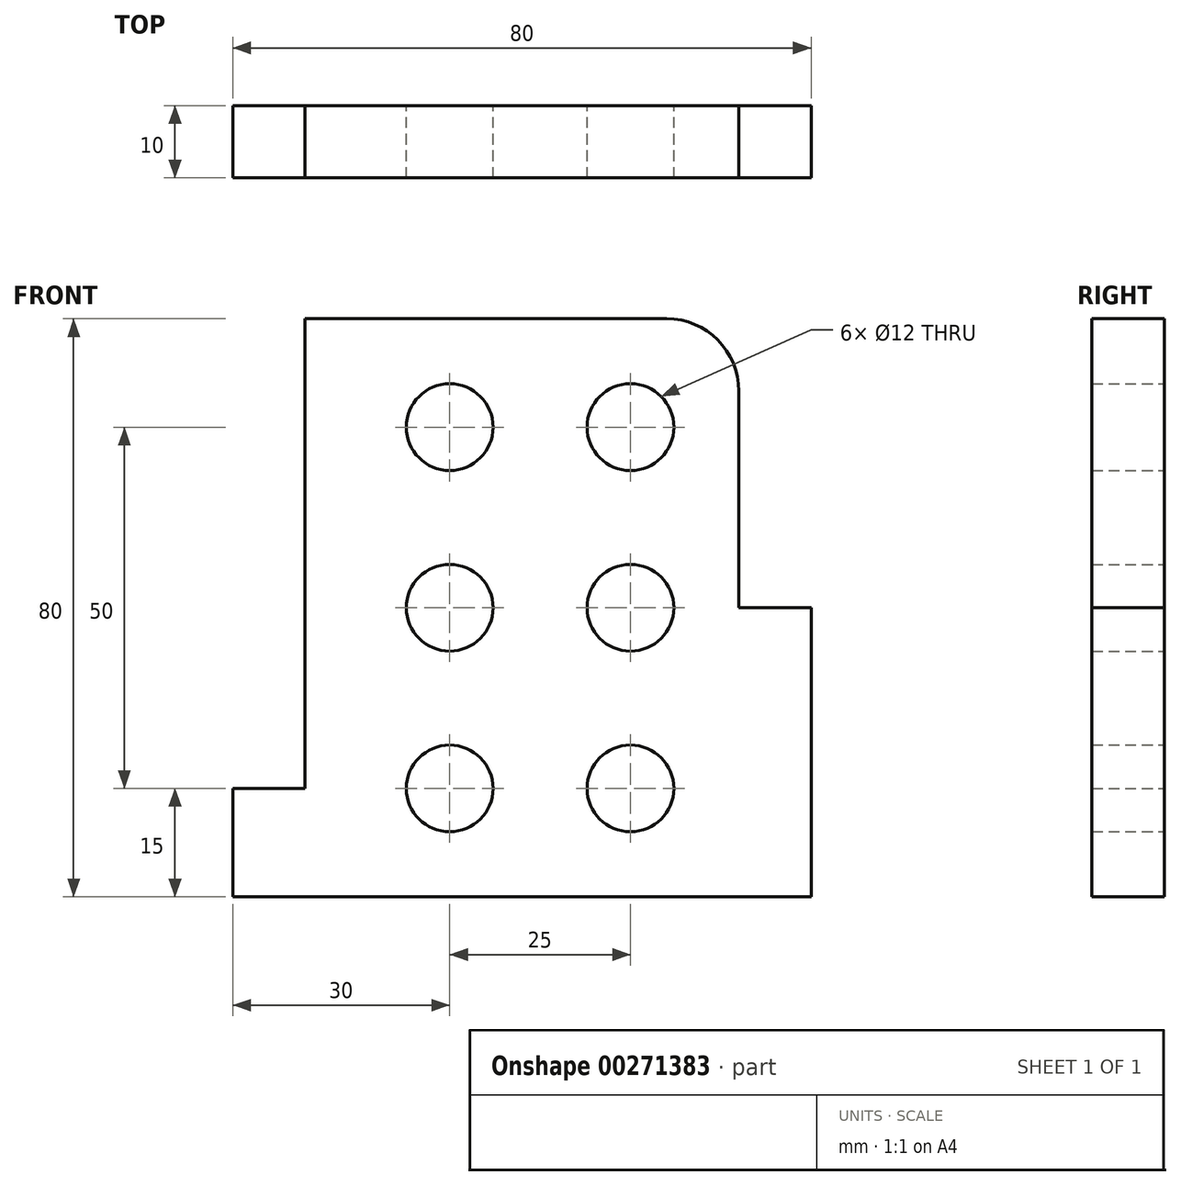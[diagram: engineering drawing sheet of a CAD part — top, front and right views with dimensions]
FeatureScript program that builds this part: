
annotation { "Feature Type Name" : "Feature", "Feature Type Description" : "" }
export const myFeature = defineFeature(function(context is Context, id is Id, definition is map)
    precondition{}
    {
        {
            var Q0;
            Q0=qCreatedBy(makeId("Front.planeOp"),FACE);
            var sketch = newSketch(context, id + "F0", { "sketchPlane" : qUnion([Q0])});
            skLineSegment(sketch, "E0", {"start": v(0, 0) * mm, "end": v(0, 15) * mm});
            skLineSegment(sketch, "E1", {"start": v(0, 15) * mm, "end": v(0, 15) * mm});
            skArc(sketch, "E2", {"start": v(70, 70) * mm, "mid": v(67.07, 77.07) * mm, "end": v(60, 80) * mm});
            skLineSegment(sketch, "E3", {"start": v(70, 70) * mm, "end": v(70, 40) * mm});
            skLineSegment(sketch, "E4", {"start": v(70, 40) * mm, "end": v(80, 40) * mm});
            skLineSegment(sketch, "E5", {"start": v(80, 40) * mm, "end": v(80, 0) * mm});
            skLineSegment(sketch, "E6", {"start": v(80, 0) * mm, "end": v(0, 0) * mm});
            skCircle(sketch, "E7", {"center": v(30, 65) * mm, "radius": 6 * mm});
            skCircle(sketch, "E8", {"center": v(55, 65) * mm, "radius": 6 * mm});
            skCircle(sketch, "E9", {"center": v(30, 40) * mm, "radius": 6 * mm});
            skCircle(sketch, "E10", {"center": v(55, 40) * mm, "radius": 6 * mm});
            skCircle(sketch, "E11", {"center": v(30, 15) * mm, "radius": 6 * mm});
            skCircle(sketch, "E12", {"center": v(55, 15) * mm, "radius": 6 * mm});
            skLineSegment(sketch, "E13", {"start": v(0, 15) * mm, "end": v(10, 15) * mm});
            skLineSegment(sketch, "E14", {"start": v(10, 15) * mm, "end": v(10, 80) * mm});
            skLineSegment(sketch, "E15", {"start": v(10, 80) * mm, "end": v(60, 80) * mm});
            skSolve(sketch);
        }
        {
            var Q0;
            Q0 = qSketchRegion(id + "F0", true);
            var Q1;
            Q1=makeQuery(id+"F0.imprint","IMPRINT",FACE,{"disambiguationData":[TD([[makeQuery(id+"F0.imprint","IMPRINT",EDGE,{"derivedFrom":sQuery(id+"F0.wireOp",EDGE,"E0")}),-1.0]])]});
            extrude(context, id + "F1", {"entities" : qUnion([Q0, Q1]), "depth" : 10 * mm});
        }
    });
